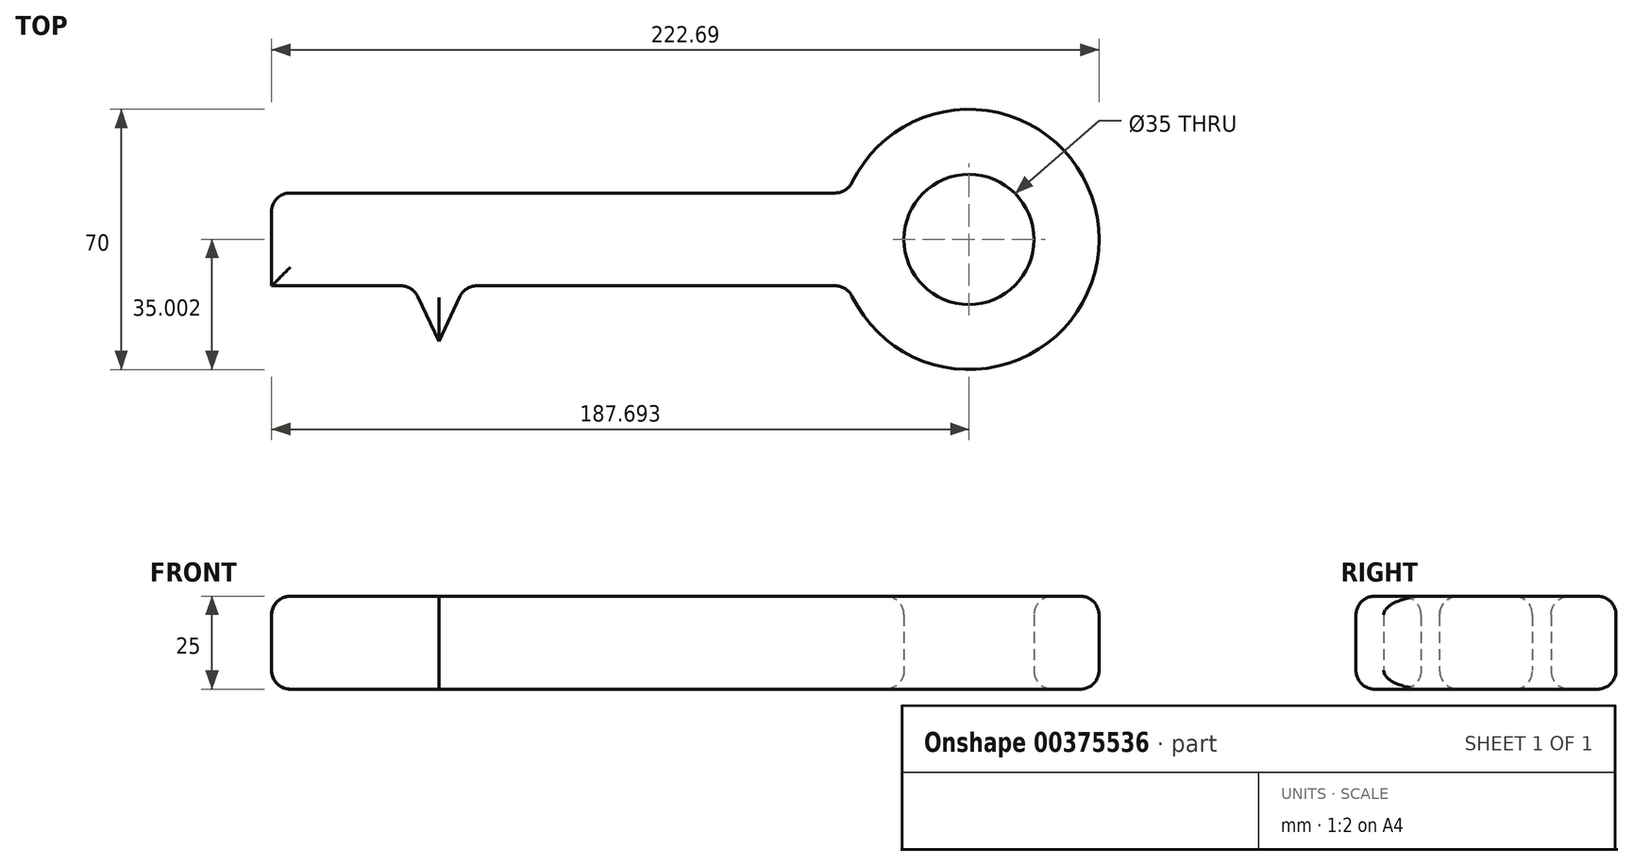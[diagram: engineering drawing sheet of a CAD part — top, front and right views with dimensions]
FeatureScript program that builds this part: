
annotation { "Feature Type Name" : "Feature", "Feature Type Description" : "" }
export const myFeature = defineFeature(function(context is Context, id is Id, definition is map)
    precondition{}
    {
        {
            var Q0;
            Q0=qCreatedBy(makeId("Top.planeOp"),FACE);
            var sketch = newSketch(context, id + "F0", { "sketchPlane" : qUnion([Q0])});
            skLineSegment(sketch, "E0.bottom", {"start": v(-67.5, 16.4) * mm, "end": v(87.5, 16.4) * mm});
            skLineSegment(sketch, "E0.top", {"start": v(-67.5, -8.6) * mm, "end": v(87.5, -8.6) * mm});
            skLineSegment(sketch, "E0.left", {"start": v(-67.5, 16.4) * mm, "end": v(-67.5, -8.6) * mm});
            skLineSegment(sketch, "E0.right", {"start": v(87.5, 16.4) * mm, "end": v(87.5, -8.6) * mm});
            skLineSegment(sketch, "E1.bottom", {"start": v(-67.5, -8.6) * mm, "end": v(-57.5, -8.6) * mm});
            skLineSegment(sketch, "E1.top", {"start": v(-67.5, -38.6) * mm, "end": v(-57.5, -38.6) * mm});
            skLineSegment(sketch, "E1.left", {"start": v(-67.5, -8.6) * mm, "end": v(-67.5, -38.6) * mm});
            skLineSegment(sketch, "E1.right", {"start": v(-57.5, -8.6) * mm, "end": v(-57.5, -38.6) * mm});
            skLineSegment(sketch, "E2.bottom", {"start": v(-47.5, -8.6) * mm, "end": v(-39.5, -8.6) * mm});
            skLineSegment(sketch, "E2.top", {"start": v(-47.5, -23.6) * mm, "end": v(-39.5, -23.6) * mm});
            skLineSegment(sketch, "E2.left", {"start": v(-47.5, -8.6) * mm, "end": v(-47.5, -23.6) * mm});
            skLineSegment(sketch, "E2.right", {"start": v(-39.5, -8.6) * mm, "end": v(-39.5, -23.6) * mm});
            skLineSegment(sketch, "E3", {"start": v(-29.5, -8.6) * mm, "end": v(-22.5, -23.6) * mm});
            skLineSegment(sketch, "E4", {"start": v(-22.5, -23.6) * mm, "end": v(-15.5, -8.6) * mm});
            skArc(sketch, "E5", {"start": v(87.5, -8.6) * mm, "mid": v(155.2, 3.9) * mm, "end": v(87.5, 16.4) * mm});
            skCircle(sketch, "E6", {"center": v(120.2, 3.9) * mm, "radius": 17.5 * mm});
            skSolve(sketch);
        }
        {
            var Q0;
            Q0=makeQuery(id+"F0.imprint","IMPRINT",FACE,{"disambiguationData":[TD([[makeQuery(id+"F0.imprint","IMPRINT",EDGE,{"derivedFrom":sQuery(id+"F0.wireOp",EDGE,"E1.bottom")}),-1.0]])]});
            var Q1;
            Q1=makeQuery(id+"F0.imprint","IMPRINT",FACE,{"disambiguationData":[TD([[makeQuery(id+"F0.imprint","IMPRINT",EDGE,{"derivedFrom":sQuery(id+"F0.wireOp",EDGE,"E2.bottom")}),-1.0]])]});
            var Q2;
            Q2=makeQuery(id+"F0.imprint","IMPRINT",FACE,{"disambiguationData":[TD([[makeQuery(id+"F0.imprint","IMPRINT",EDGE,{"derivedFrom":sQuery(id+"F0.wireOp",EDGE,"E0.bottom")}),-1.0]])]});
            var Q3;
            {var subQ0=sQuery(id+"F0.wireOp",EDGE,"E3");Q3=makeQuery(id+"F0.imprint","IMPRINT",FACE,{"disambiguationData":[TD([[makeQuery(id+"F0.imprint","IMPRINT",EDGE,{"derivedFrom":subQ0}),1.0]])]});}
            var Q4;
            Q4=makeQuery(id+"F0.imprint","IMPRINT",FACE,{"disambiguationData":[TD([[makeQuery(id+"F0.imprint","IMPRINT",EDGE,{"derivedFrom":sQuery(id+"F0.wireOp",EDGE,"E0.right")}),1.0]])]});
            extrude(context, id + "F1", {"entities" : qUnion([Q0, Q1, Q2, Q3, Q4]), "depth" : 25 * mm});
        }
        {
            var Q0;
            Q0=makeQuery(id+"F1.opExtrude","CAP_FACE",FACE,{"disambiguationData":[OSD([sQuery(id+"F0.wireOp",EDGE,"E0.bottom"),sQuery(id+"F0.wireOp",EDGE,"E0.top"),sQuery(id+"F0.wireOp",EDGE,"E0.left"),sQuery(id+"F0.wireOp",EDGE,"E1.top"),sQuery(id+"F0.wireOp",EDGE,"E1.left"),sQuery(id+"F0.wireOp",EDGE,"E1.right"),sQuery(id+"F0.wireOp",EDGE,"E2.top"),sQuery(id+"F0.wireOp",EDGE,"E2.left"),sQuery(id+"F0.wireOp",EDGE,"E2.right"),sQuery(id+"F0.wireOp",EDGE,"E3"),sQuery(id+"F0.wireOp",EDGE,"E4"),sQuery(id+"F0.wireOp",EDGE,"E5"),sQuery(id+"F0.wireOp",EDGE,"E6")])],"isStart":false});
            var Q1;
            Q1=makeQuery(id+"F1.opExtrude","SWEPT_FACE",FACE,{"disambiguationData":[OSD([sQuery(id+"F0.wireOp",EDGE,"E5")])]});
            var Q2;
            Q2=makeQuery(id+"F1.opExtrude","SWEPT_FACE",FACE,{"disambiguationData":[OSD([sQuery(id+"F0.wireOp",EDGE,"E0.bottom")])]});
            var Q3;
            {var subQ0=sQuery(id+"F0.wireOp",EDGE,"E0.top");Q3=makeQuery(id+"F1.opExtrude","SWEPT_FACE",FACE,{"disambiguationData":[OSD([subQ0]),TDD([makeQuery(id+"F0.imprint","IMPRINT",EDGE,{"disambiguationData":[TD([[makeQuery(id+"F0.imprint","INTERSECT",VERTEX,{"derivedFrom":[subQ0,sQuery(id+"F0.wireOp",EDGE,"E4")]}),-1.0]])],"derivedFrom":subQ0})])]});}
            var Q4;
            Q4=makeQuery(id+"F1.opExtrude","SWEPT_EDGE",EDGE,{"disambiguationData":[OSD([sQuery(id+"F0.wireOp",EDGE,"E0.top"),sQuery(id+"F0.wireOp",EDGE,"E3")])]});
            var Q5;
            Q5=makeQuery(id+"F1.opExtrude","SWEPT_FACE",FACE,{"disambiguationData":[OSD([sQuery(id+"F0.wireOp",EDGE,"E2.top")])]});
            var Q6;
            Q6=makeQuery(id+"F1.opExtrude","SWEPT_EDGE",EDGE,{"disambiguationData":[OSD([sQuery(id+"F0.wireOp",EDGE,"E1.top"),sQuery(id+"F0.wireOp",EDGE,"E1.right")])]});
            fillet(context, id + "F2", {"entities" : qUnion([Q0, Q1, Q2, Q3, Q4, Q5, Q6]), "radius" : 5 * mm, "tangentPropagation" : true, "allowEdgeOverflow" : false});
        }
        {
            var Q0;
            Q0=makeQuery(id+"F1.opExtrude","CAP_FACE",FACE,{"disambiguationData":[OSD([sQuery(id+"F0.wireOp",EDGE,"E0.bottom"),sQuery(id+"F0.wireOp",EDGE,"E0.top"),sQuery(id+"F0.wireOp",EDGE,"E0.left"),sQuery(id+"F0.wireOp",EDGE,"E1.top"),sQuery(id+"F0.wireOp",EDGE,"E1.left"),sQuery(id+"F0.wireOp",EDGE,"E1.right"),sQuery(id+"F0.wireOp",EDGE,"E2.top"),sQuery(id+"F0.wireOp",EDGE,"E2.left"),sQuery(id+"F0.wireOp",EDGE,"E2.right"),sQuery(id+"F0.wireOp",EDGE,"E3"),sQuery(id+"F0.wireOp",EDGE,"E4"),sQuery(id+"F0.wireOp",EDGE,"E5"),sQuery(id+"F0.wireOp",EDGE,"E6")])],"isStart":true});
            fillet(context, id + "F3", {"entities" : qUnion([Q0]), "radius" : 5 * mm, "tangentPropagation" : true, "allowEdgeOverflow" : false});
        }
    });
